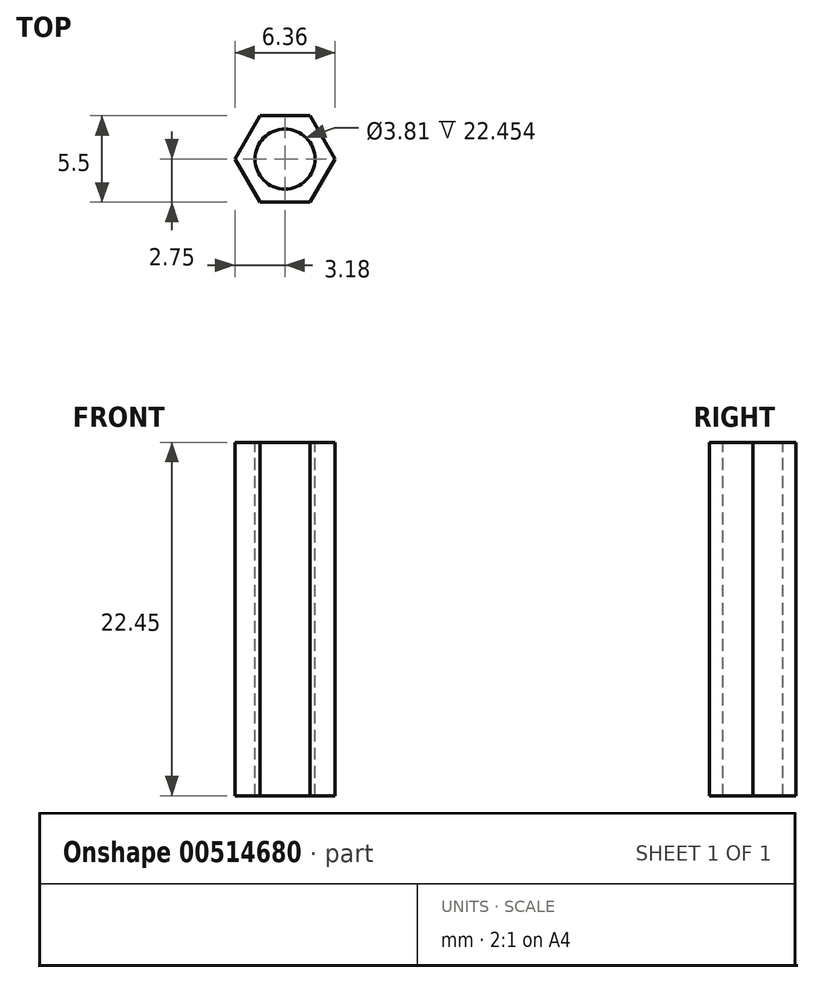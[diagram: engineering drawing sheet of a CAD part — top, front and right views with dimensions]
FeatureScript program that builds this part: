
annotation { "Feature Type Name" : "Feature", "Feature Type Description" : "" }
export const myFeature = defineFeature(function(context is Context, id is Id, definition is map)
    precondition{}
    {
        {
            var Q0;
            Q0=qCreatedBy(makeId("Top.planeOp"),FACE);
            var sketch = newSketch(context, id + "F0", { "sketchPlane" : qUnion([Q0])});
            skCircle(sketch, "E0", {"center": v(0, 0) * mm, "radius": 3.18 * mm});
            skCircle(sketch, "E1.cCircle", {"center": v(0, 0) * mm, "radius": 3.18 * mm, "construction": true});
            skLineSegment(sketch, "E1.0", {"start": v(3.18, 0) * mm, "end": v(1.59, -2.75) * mm});
            skLineSegment(sketch, "E1.1", {"start": v(1.59, -2.75) * mm, "end": v(-1.59, -2.75) * mm});
            skLineSegment(sketch, "E1.2", {"start": v(-1.59, -2.75) * mm, "end": v(-3.18, 0) * mm});
            skLineSegment(sketch, "E1.3", {"start": v(-3.18, 0) * mm, "end": v(-1.59, 2.75) * mm});
            skLineSegment(sketch, "E1.4", {"start": v(-1.59, 2.75) * mm, "end": v(1.59, 2.75) * mm});
            skLineSegment(sketch, "E1.5", {"start": v(1.59, 2.75) * mm, "end": v(3.18, 0) * mm});
            skSolve(sketch);
        }
        {
            var Q0;
            Q0=makeQuery(id+"F0.imprint","IMPRINT",FACE,{"disambiguationData":[TD([[makeQuery(id+"F0.imprint","IMPRINT",EDGE,{"derivedFrom":sQuery(id+"F0.wireOp",EDGE,"E1.0")}),-1.0]])]});
            extrude(context, id + "F1", {"entities" : qUnion([Q0]), "depth" : 22.45 * mm, "offsetDistance" : 25.4 * mm});
        }
        {
            var Q0;
            Q0=makeQuery(id+"F1.opExtrude","CAP_FACE",FACE,{"disambiguationData":[OSD([sQuery(id+"F0.wireOp",EDGE,"E1.0"),sQuery(id+"F0.wireOp",EDGE,"E1.1"),sQuery(id+"F0.wireOp",EDGE,"E1.2"),sQuery(id+"F0.wireOp",EDGE,"E1.3"),sQuery(id+"F0.wireOp",EDGE,"E1.4"),sQuery(id+"F0.wireOp",EDGE,"E1.5")])],"isStart":false});
            var sketch = newSketch(context, id + "F2", { "sketchPlane" : qUnion([Q0])});
            skCircle(sketch, "E2", {"center": v(0, 0) * mm, "radius": 1.9 * mm});
            skSolve(sketch);
        }
        {
            var Q0;
            Q0=makeQuery(id+"F2.imprint","IMPRINT",FACE,{"disambiguationData":[TD([[makeQuery(id+"F2.imprint","IMPRINT",EDGE,{"derivedFrom":sQuery(id+"F2.wireOp",EDGE,"E2")}),1.0]])]});
            extrude(context, id + "F3", {"entities" : qUnion([Q0]), "operationType" : NewBodyOperationType.REMOVE, "endBound" : BoundingType.UP_TO_NEXT, "oppositeDirection" : true, "depth" : 25.4 * mm, "offsetDistance" : 25.4 * mm});
        }
    });
